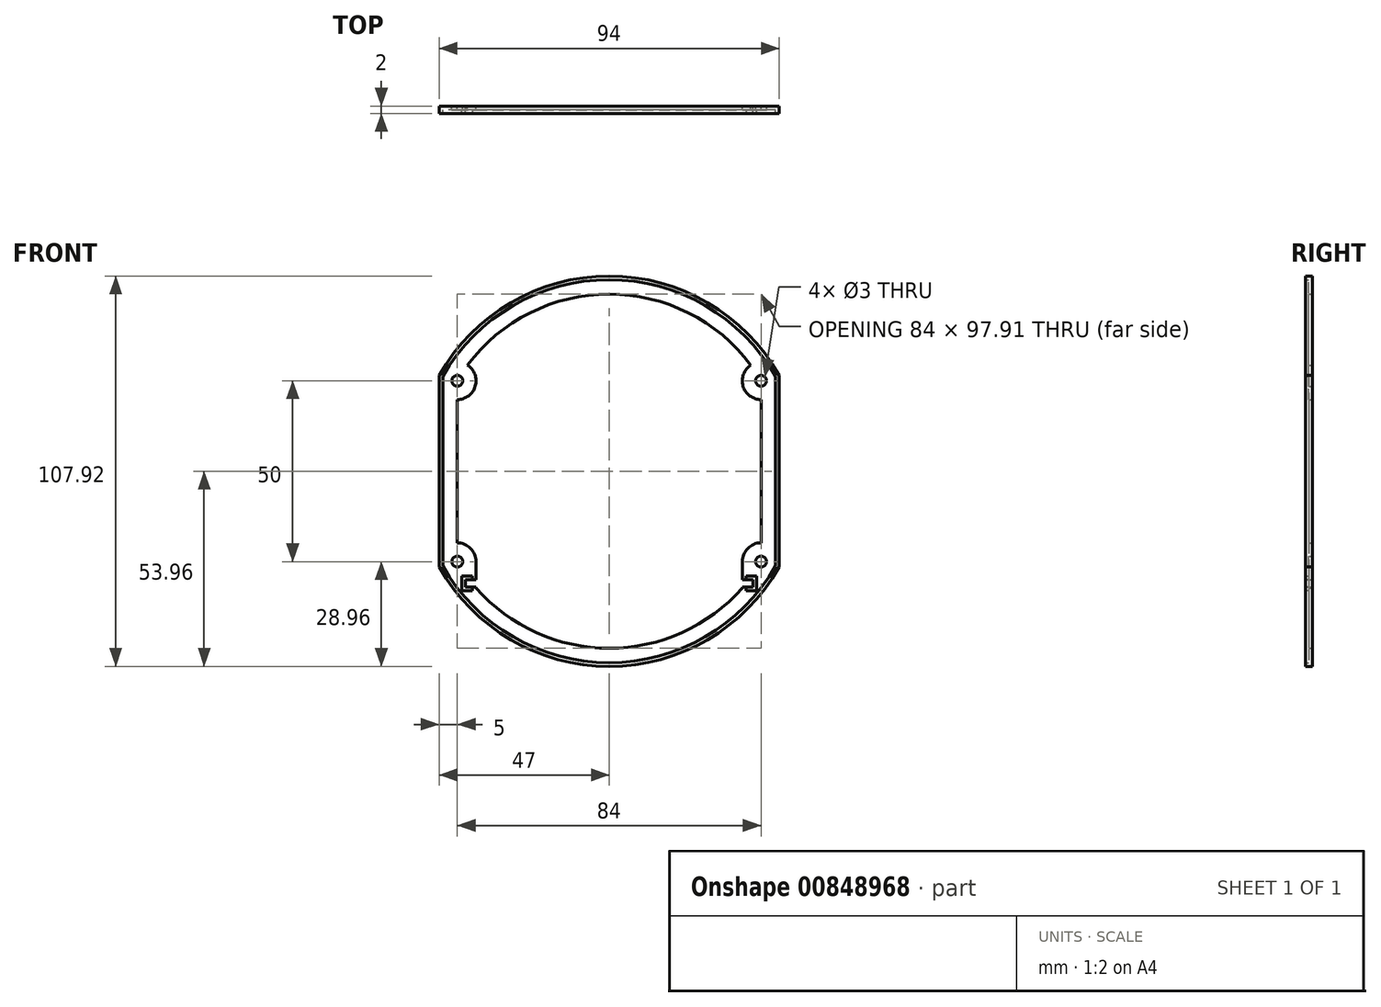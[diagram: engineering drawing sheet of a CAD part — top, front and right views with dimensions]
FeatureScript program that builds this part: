
annotation { "Feature Type Name" : "Feature", "Feature Type Description" : "" }
export const myFeature = defineFeature(function(context is Context, id is Id, definition is map)
    precondition{}
    {
        {
            var Q0;
            Q0=qCreatedBy(makeId("Front.planeOp"),FACE);
            var sketch = newSketch(context, id + "F0", { "sketchPlane" : qUnion([Q0])});
            skPoint(sketch, "E0.middle", {"position": v(0, 0) * mm});
            skCircle(sketch, "E1", {"center": v(-42, 25) * mm, "radius": 1.5 * mm});
            skLineSegment(sketch, "E2.left", {"start": v(-47, 26.5) * mm, "end": v(-47, -26.5) * mm});
            skLineSegment(sketch, "E2.right", {"start": v(47, 26.5) * mm, "end": v(47, -26.5) * mm});
            skArc(sketch, "E3", {"start": v(-39.17, 29.36) * mm, "mid": v(-21.9, 43.78) * mm, "end": v(0, 48.96) * mm});
            skArc(sketch, "E4", {"start": v(-47, 26.5) * mm, "mid": v(-27.22, 46.59) * mm, "end": v(0, 53.96) * mm});
            skArc(sketch, "E5", {"start": v(-39.17, 29.36) * mm, "mid": v(-37.01, 23.53) * mm, "end": v(-42, 19.8) * mm});
            skCircle(sketch, "E6", {"center": v(-42, -25) * mm, "radius": 1.5 * mm});
            skArc(sketch, "E7", {"start": v(-47, -26.5) * mm, "mid": v(-27.22, -46.59) * mm, "end": v(0, -53.96) * mm});
            skLineSegment(sketch, "E8.left", {"start": v(-36.8, -25) * mm, "end": v(-36.8, -30) * mm});
            skLineSegment(sketch, "E9.bottom", {"start": v(-36.8, -30) * mm, "end": v(-39.8, -30) * mm});
            skLineSegment(sketch, "E9.top", {"start": v(-36.8, -32) * mm, "end": v(-39.8, -32) * mm});
            skLineSegment(sketch, "E9.right", {"start": v(-39.8, -30) * mm, "end": v(-39.8, -32) * mm});
            skArc(sketch, "E10", {"start": v(-36.8, -25) * mm, "mid": v(-38.32, -21.32) * mm, "end": v(-42, -19.8) * mm});
            skLineSegment(sketch, "E11", {"start": v(-37.05, -32) * mm, "end": v(-36.8, -32) * mm});
            skLineSegment(sketch, "E12", {"start": v(-36.8, -32.29) * mm, "end": v(-36.8, -32) * mm});
            skArc(sketch, "E13", {"start": v(-36.8, -32.29) * mm, "mid": v(-20.2, -44.6) * mm, "end": v(0, -48.96) * mm});
            skLineSegment(sketch, "E14", {"start": v(-42, 19.8) * mm, "end": v(-42, -19.8) * mm});
            skLineSegment(sketch, "E15", {"start": v(0, 63.92) * mm, "end": v(0, -61.44) * mm, "construction": true});
            skArc(sketch, "E16.MirrorCS", {"start": v(39.17, 29.36) * mm, "mid": v(21.9, 43.78) * mm, "end": v(0, 48.96) * mm});
            skArc(sketch, "E17.MirrorCS", {"start": v(47, 26.5) * mm, "mid": v(27.22, 46.59) * mm, "end": v(0, 53.96) * mm});
            skCircle(sketch, "E18.MirrorC", {"center": v(42, 25) * mm, "radius": 1.5 * mm});
            skArc(sketch, "E19.MirrorCS", {"start": v(39.17, 29.36) * mm, "mid": v(37.01, 23.53) * mm, "end": v(42, 19.8) * mm});
            skArc(sketch, "E20.MirrorCS", {"start": v(36.8, -25) * mm, "mid": v(38.32, -21.32) * mm, "end": v(42, -19.8) * mm});
            skLineSegment(sketch, "E21.MirrorCS", {"start": v(36.8, -25) * mm, "end": v(36.8, -30) * mm});
            skLineSegment(sketch, "E22.MirrorCS", {"start": v(36.8, -30) * mm, "end": v(39.8, -30) * mm});
            skLineSegment(sketch, "E23.MirrorCS", {"start": v(39.8, -30) * mm, "end": v(39.8, -32) * mm});
            skLineSegment(sketch, "E24.MirrorCS", {"start": v(36.8, -32) * mm, "end": v(39.8, -32) * mm});
            skLineSegment(sketch, "E25.MirrorCS", {"start": v(37.05, -32) * mm, "end": v(36.8, -32) * mm});
            skLineSegment(sketch, "E26.MirrorCS", {"start": v(36.8, -32.29) * mm, "end": v(36.8, -32) * mm});
            skLineSegment(sketch, "E27.MirrorCS", {"start": v(42, 19.8) * mm, "end": v(42, -19.8) * mm});
            skArc(sketch, "E28.MirrorCS", {"start": v(36.8, -32.29) * mm, "mid": v(20.2, -44.6) * mm, "end": v(0, -48.96) * mm});
            skArc(sketch, "E29.MirrorCS", {"start": v(47, -26.5) * mm, "mid": v(27.22, -46.59) * mm, "end": v(0, -53.96) * mm});
            skCircle(sketch, "E30.MirrorC", {"center": v(42, -25) * mm, "radius": 1.5 * mm});
            skSolve(sketch);
        }
        {
            var Q0;
            Q0=makeQuery(id+"F0.imprint","IMPRINT",FACE,{"disambiguationData":[TD([[makeQuery(id+"F0.imprint","IMPRINT",EDGE,{"derivedFrom":sQuery(id+"F0.wireOp",EDGE,"E1")}),-1.0]])]});
            extrude(context, id + "F1", {"entities" : qUnion([Q0]), "depth" : 2 * mm, "offsetDistance" : 25 * mm});
        }
        {
            var Q0;
            Q0=makeQuery(id+"F1.opExtrude","CAP_FACE",FACE,{"disambiguationData":[OSD([sQuery(id+"F0.wireOp",EDGE,"E1"),sQuery(id+"F0.wireOp",EDGE,"E2.left"),sQuery(id+"F0.wireOp",EDGE,"E2.right"),sQuery(id+"F0.wireOp",EDGE,"E3"),sQuery(id+"F0.wireOp",EDGE,"E4"),sQuery(id+"F0.wireOp",EDGE,"E5"),sQuery(id+"F0.wireOp",EDGE,"E6"),sQuery(id+"F0.wireOp",EDGE,"E7"),sQuery(id+"F0.wireOp",EDGE,"E8.left"),sQuery(id+"F0.wireOp",EDGE,"E9.bottom"),sQuery(id+"F0.wireOp",EDGE,"E9.top"),sQuery(id+"F0.wireOp",EDGE,"E9.right"),sQuery(id+"F0.wireOp",EDGE,"E10"),sQuery(id+"F0.wireOp",EDGE,"E11"),sQuery(id+"F0.wireOp",EDGE,"E12"),sQuery(id+"F0.wireOp",EDGE,"E13"),sQuery(id+"F0.wireOp",EDGE,"E14"),sQuery(id+"F0.wireOp",EDGE,"E16.MirrorCS"),sQuery(id+"F0.wireOp",EDGE,"E17.MirrorCS"),sQuery(id+"F0.wireOp",EDGE,"E18.MirrorC"),sQuery(id+"F0.wireOp",EDGE,"E19.MirrorCS"),sQuery(id+"F0.wireOp",EDGE,"E20.MirrorCS"),sQuery(id+"F0.wireOp",EDGE,"E21.MirrorCS"),sQuery(id+"F0.wireOp",EDGE,"E22.MirrorCS"),sQuery(id+"F0.wireOp",EDGE,"E23.MirrorCS"),sQuery(id+"F0.wireOp",EDGE,"E24.MirrorCS"),sQuery(id+"F0.wireOp",EDGE,"E25.MirrorCS"),sQuery(id+"F0.wireOp",EDGE,"E26.MirrorCS"),sQuery(id+"F0.wireOp",EDGE,"E27.MirrorCS"),sQuery(id+"F0.wireOp",EDGE,"E28.MirrorCS"),sQuery(id+"F0.wireOp",EDGE,"E29.MirrorCS"),sQuery(id+"F0.wireOp",EDGE,"E30.MirrorC")])],"isStart":false});
            shell(context, id + "F2", {"entities" : qUnion([Q0]), "thickness" : 1 * mm});
        }
        {
            var Q0;
            Q0=makeQuery(id+"F1.opExtrude","CAP_FACE",FACE,{"disambiguationData":[OSD([sQuery(id+"F0.wireOp",EDGE,"E1"),sQuery(id+"F0.wireOp",EDGE,"E2.left"),sQuery(id+"F0.wireOp",EDGE,"E2.right"),sQuery(id+"F0.wireOp",EDGE,"E3"),sQuery(id+"F0.wireOp",EDGE,"E4"),sQuery(id+"F0.wireOp",EDGE,"E5"),sQuery(id+"F0.wireOp",EDGE,"E6"),sQuery(id+"F0.wireOp",EDGE,"E7"),sQuery(id+"F0.wireOp",EDGE,"E8.left"),sQuery(id+"F0.wireOp",EDGE,"E9.bottom"),sQuery(id+"F0.wireOp",EDGE,"E9.top"),sQuery(id+"F0.wireOp",EDGE,"E9.right"),sQuery(id+"F0.wireOp",EDGE,"E10"),sQuery(id+"F0.wireOp",EDGE,"E11"),sQuery(id+"F0.wireOp",EDGE,"E12"),sQuery(id+"F0.wireOp",EDGE,"E13"),sQuery(id+"F0.wireOp",EDGE,"E14"),sQuery(id+"F0.wireOp",EDGE,"E16.MirrorCS"),sQuery(id+"F0.wireOp",EDGE,"E17.MirrorCS"),sQuery(id+"F0.wireOp",EDGE,"E18.MirrorC"),sQuery(id+"F0.wireOp",EDGE,"E19.MirrorCS"),sQuery(id+"F0.wireOp",EDGE,"E20.MirrorCS"),sQuery(id+"F0.wireOp",EDGE,"E21.MirrorCS"),sQuery(id+"F0.wireOp",EDGE,"E22.MirrorCS"),sQuery(id+"F0.wireOp",EDGE,"E23.MirrorCS"),sQuery(id+"F0.wireOp",EDGE,"E24.MirrorCS"),sQuery(id+"F0.wireOp",EDGE,"E25.MirrorCS"),sQuery(id+"F0.wireOp",EDGE,"E26.MirrorCS"),sQuery(id+"F0.wireOp",EDGE,"E27.MirrorCS"),sQuery(id+"F0.wireOp",EDGE,"E28.MirrorCS"),sQuery(id+"F0.wireOp",EDGE,"E29.MirrorCS"),sQuery(id+"F0.wireOp",EDGE,"E30.MirrorC")])],"isStart":false});
            var sketch = newSketch(context, id + "F3", { "sketchPlane" : qUnion([Q0])});
            skLineSegment(sketch, "E31.bottom", {"start": v(-40.8, -29) * mm, "end": v(-37.8, -29) * mm});
            skLineSegment(sketch, "E31.top", {"start": v(-40.8, -33) * mm, "end": v(-37.8, -33) * mm});
            skLineSegment(sketch, "E31.left", {"start": v(-40.8, -29) * mm, "end": v(-40.8, -33) * mm});
            skLineSegment(sketch, "E31.right", {"start": v(-37.8, -29) * mm, "end": v(-37.8, -33) * mm});
            skLineSegment(sketch, "E32.bottom", {"start": v(40.8, -29) * mm, "end": v(37.8, -29) * mm});
            skLineSegment(sketch, "E32.top", {"start": v(40.8, -33) * mm, "end": v(37.8, -33) * mm});
            skLineSegment(sketch, "E32.left", {"start": v(40.8, -29) * mm, "end": v(40.8, -33) * mm});
            skLineSegment(sketch, "E32.right", {"start": v(37.8, -29) * mm, "end": v(37.8, -33) * mm});
            skSolve(sketch);
        }
        {
            var Q0;
            {var subQ0=sQuery(id+"F0.wireOp",EDGE,"E30.MirrorC");var subQ1=sQuery(id+"F0.wireOp",EDGE,"E29.MirrorCS");var subQ2=sQuery(id+"F0.wireOp",EDGE,"E28.MirrorCS");var subQ3=sQuery(id+"F0.wireOp",EDGE,"E27.MirrorCS");var subQ4=sQuery(id+"F0.wireOp",EDGE,"E26.MirrorCS");var subQ5=sQuery(id+"F0.wireOp",EDGE,"E25.MirrorCS");var subQ6=sQuery(id+"F0.wireOp",EDGE,"E24.MirrorCS");var subQ7=sQuery(id+"F0.wireOp",EDGE,"E23.MirrorCS");var subQ8=sQuery(id+"F0.wireOp",EDGE,"E22.MirrorCS");var subQ9=sQuery(id+"F0.wireOp",EDGE,"E21.MirrorCS");var subQ10=sQuery(id+"F0.wireOp",EDGE,"E20.MirrorCS");var subQ11=sQuery(id+"F0.wireOp",EDGE,"E19.MirrorCS");var subQ12=sQuery(id+"F0.wireOp",EDGE,"E18.MirrorC");var subQ13=sQuery(id+"F0.wireOp",EDGE,"E17.MirrorCS");var subQ14=sQuery(id+"F0.wireOp",EDGE,"E16.MirrorCS");var subQ15=sQuery(id+"F0.wireOp",EDGE,"E14");var subQ16=sQuery(id+"F0.wireOp",EDGE,"E13");var subQ17=sQuery(id+"F0.wireOp",EDGE,"E12");var subQ18=sQuery(id+"F0.wireOp",EDGE,"E11");var subQ19=sQuery(id+"F0.wireOp",EDGE,"E10");var subQ20=sQuery(id+"F0.wireOp",EDGE,"E9.right");var subQ21=sQuery(id+"F0.wireOp",EDGE,"E9.top");var subQ22=sQuery(id+"F0.wireOp",EDGE,"E9.bottom");var subQ23=sQuery(id+"F0.wireOp",EDGE,"E8.left");var subQ24=sQuery(id+"F0.wireOp",EDGE,"E7");var subQ25=sQuery(id+"F0.wireOp",EDGE,"E6");var subQ26=sQuery(id+"F0.wireOp",EDGE,"E5");var subQ27=sQuery(id+"F0.wireOp",EDGE,"E4");var subQ28=sQuery(id+"F0.wireOp",EDGE,"E3");var subQ29=sQuery(id+"F0.wireOp",EDGE,"E2.right");var subQ30=sQuery(id+"F0.wireOp",EDGE,"E2.left");var subQ31=sQuery(id+"F0.wireOp",EDGE,"E1");Q0=makeQuery(id+"F2.opShell","OFFSET_FACE",FACE,{"disambiguationData":[OSD([subQ31,subQ30,subQ29,subQ28,subQ27,subQ26,subQ25,subQ24,subQ23,subQ22,subQ21,subQ20,subQ19,subQ18,subQ17,subQ16,subQ15,subQ14,subQ13,subQ12,subQ11,subQ10,subQ9,subQ8,subQ7,subQ6,subQ5,subQ4,subQ3,subQ2,subQ1,subQ0]),TDD([makeQuery(id+"F1.opExtrude","CAP_FACE",FACE,{"disambiguationData":[OSD([subQ31,subQ30,subQ29,subQ28,subQ27,subQ26,subQ25,subQ24,subQ23,subQ22,subQ21,subQ20,subQ19,subQ18,subQ17,subQ16,subQ15,subQ14,subQ13,subQ12,subQ11,subQ10,subQ9,subQ8,subQ7,subQ6,subQ5,subQ4,subQ3,subQ2,subQ1,subQ0])],"isStart":false})]),OD(0.0)]});}
            var Q1;
            {var subQ0=sQuery(id+"F0.wireOp",EDGE,"E30.MirrorC");var subQ1=sQuery(id+"F0.wireOp",EDGE,"E29.MirrorCS");var subQ2=sQuery(id+"F0.wireOp",EDGE,"E28.MirrorCS");var subQ3=sQuery(id+"F0.wireOp",EDGE,"E27.MirrorCS");var subQ4=sQuery(id+"F0.wireOp",EDGE,"E26.MirrorCS");var subQ5=sQuery(id+"F0.wireOp",EDGE,"E25.MirrorCS");var subQ6=sQuery(id+"F0.wireOp",EDGE,"E24.MirrorCS");var subQ7=sQuery(id+"F0.wireOp",EDGE,"E23.MirrorCS");var subQ8=sQuery(id+"F0.wireOp",EDGE,"E22.MirrorCS");var subQ9=sQuery(id+"F0.wireOp",EDGE,"E21.MirrorCS");var subQ10=sQuery(id+"F0.wireOp",EDGE,"E20.MirrorCS");var subQ11=sQuery(id+"F0.wireOp",EDGE,"E19.MirrorCS");var subQ12=sQuery(id+"F0.wireOp",EDGE,"E18.MirrorC");var subQ13=sQuery(id+"F0.wireOp",EDGE,"E17.MirrorCS");var subQ14=sQuery(id+"F0.wireOp",EDGE,"E16.MirrorCS");var subQ15=sQuery(id+"F0.wireOp",EDGE,"E14");var subQ16=sQuery(id+"F0.wireOp",EDGE,"E13");var subQ17=sQuery(id+"F0.wireOp",EDGE,"E12");var subQ18=sQuery(id+"F0.wireOp",EDGE,"E11");var subQ19=sQuery(id+"F0.wireOp",EDGE,"E10");var subQ20=sQuery(id+"F0.wireOp",EDGE,"E9.right");var subQ21=sQuery(id+"F0.wireOp",EDGE,"E9.top");var subQ22=sQuery(id+"F0.wireOp",EDGE,"E9.bottom");var subQ23=sQuery(id+"F0.wireOp",EDGE,"E8.left");var subQ24=sQuery(id+"F0.wireOp",EDGE,"E7");var subQ25=sQuery(id+"F0.wireOp",EDGE,"E6");var subQ26=sQuery(id+"F0.wireOp",EDGE,"E5");var subQ27=sQuery(id+"F0.wireOp",EDGE,"E4");var subQ28=sQuery(id+"F0.wireOp",EDGE,"E3");var subQ29=sQuery(id+"F0.wireOp",EDGE,"E2.right");var subQ30=sQuery(id+"F0.wireOp",EDGE,"E2.left");var subQ31=sQuery(id+"F0.wireOp",EDGE,"E1");Q1=makeQuery(id+"F2.opShell","OFFSET_FACE",FACE,{"disambiguationData":[OSD([subQ31,subQ30,subQ29,subQ28,subQ27,subQ26,subQ25,subQ24,subQ23,subQ22,subQ21,subQ20,subQ19,subQ18,subQ17,subQ16,subQ15,subQ14,subQ13,subQ12,subQ11,subQ10,subQ9,subQ8,subQ7,subQ6,subQ5,subQ4,subQ3,subQ2,subQ1,subQ0]),TDD([makeQuery(id+"F1.opExtrude","CAP_FACE",FACE,{"disambiguationData":[OSD([subQ31,subQ30,subQ29,subQ28,subQ27,subQ26,subQ25,subQ24,subQ23,subQ22,subQ21,subQ20,subQ19,subQ18,subQ17,subQ16,subQ15,subQ14,subQ13,subQ12,subQ11,subQ10,subQ9,subQ8,subQ7,subQ6,subQ5,subQ4,subQ3,subQ2,subQ1,subQ0])],"isStart":false})]),OD(3.0)]});}
            var Q2;
            {var subQ0=sQuery(id+"F0.wireOp",EDGE,"E30.MirrorC");var subQ1=sQuery(id+"F0.wireOp",EDGE,"E29.MirrorCS");var subQ2=sQuery(id+"F0.wireOp",EDGE,"E28.MirrorCS");var subQ3=sQuery(id+"F0.wireOp",EDGE,"E27.MirrorCS");var subQ4=sQuery(id+"F0.wireOp",EDGE,"E26.MirrorCS");var subQ5=sQuery(id+"F0.wireOp",EDGE,"E25.MirrorCS");var subQ6=sQuery(id+"F0.wireOp",EDGE,"E24.MirrorCS");var subQ7=sQuery(id+"F0.wireOp",EDGE,"E23.MirrorCS");var subQ8=sQuery(id+"F0.wireOp",EDGE,"E22.MirrorCS");var subQ9=sQuery(id+"F0.wireOp",EDGE,"E21.MirrorCS");var subQ10=sQuery(id+"F0.wireOp",EDGE,"E20.MirrorCS");var subQ11=sQuery(id+"F0.wireOp",EDGE,"E19.MirrorCS");var subQ12=sQuery(id+"F0.wireOp",EDGE,"E18.MirrorC");var subQ13=sQuery(id+"F0.wireOp",EDGE,"E17.MirrorCS");var subQ14=sQuery(id+"F0.wireOp",EDGE,"E16.MirrorCS");var subQ15=sQuery(id+"F0.wireOp",EDGE,"E14");var subQ16=sQuery(id+"F0.wireOp",EDGE,"E13");var subQ17=sQuery(id+"F0.wireOp",EDGE,"E12");var subQ18=sQuery(id+"F0.wireOp",EDGE,"E11");var subQ19=sQuery(id+"F0.wireOp",EDGE,"E10");var subQ20=sQuery(id+"F0.wireOp",EDGE,"E9.right");var subQ21=sQuery(id+"F0.wireOp",EDGE,"E9.top");var subQ22=sQuery(id+"F0.wireOp",EDGE,"E9.bottom");var subQ23=sQuery(id+"F0.wireOp",EDGE,"E8.left");var subQ24=sQuery(id+"F0.wireOp",EDGE,"E7");var subQ25=sQuery(id+"F0.wireOp",EDGE,"E6");var subQ26=sQuery(id+"F0.wireOp",EDGE,"E5");var subQ27=sQuery(id+"F0.wireOp",EDGE,"E4");var subQ28=sQuery(id+"F0.wireOp",EDGE,"E3");var subQ29=sQuery(id+"F0.wireOp",EDGE,"E2.right");var subQ30=sQuery(id+"F0.wireOp",EDGE,"E2.left");var subQ31=sQuery(id+"F0.wireOp",EDGE,"E1");Q2=makeQuery(id+"F2.opShell","OFFSET_FACE",FACE,{"disambiguationData":[OSD([subQ31,subQ30,subQ29,subQ28,subQ27,subQ26,subQ25,subQ24,subQ23,subQ22,subQ21,subQ20,subQ19,subQ18,subQ17,subQ16,subQ15,subQ14,subQ13,subQ12,subQ11,subQ10,subQ9,subQ8,subQ7,subQ6,subQ5,subQ4,subQ3,subQ2,subQ1,subQ0]),TDD([makeQuery(id+"F1.opExtrude","CAP_FACE",FACE,{"disambiguationData":[OSD([subQ31,subQ30,subQ29,subQ28,subQ27,subQ26,subQ25,subQ24,subQ23,subQ22,subQ21,subQ20,subQ19,subQ18,subQ17,subQ16,subQ15,subQ14,subQ13,subQ12,subQ11,subQ10,subQ9,subQ8,subQ7,subQ6,subQ5,subQ4,subQ3,subQ2,subQ1,subQ0])],"isStart":false})]),OD(4.0)]});}
            var Q3;
            {var subQ0=sQuery(id+"F0.wireOp",EDGE,"E30.MirrorC");var subQ1=sQuery(id+"F0.wireOp",EDGE,"E29.MirrorCS");var subQ2=sQuery(id+"F0.wireOp",EDGE,"E28.MirrorCS");var subQ3=sQuery(id+"F0.wireOp",EDGE,"E27.MirrorCS");var subQ4=sQuery(id+"F0.wireOp",EDGE,"E26.MirrorCS");var subQ5=sQuery(id+"F0.wireOp",EDGE,"E25.MirrorCS");var subQ6=sQuery(id+"F0.wireOp",EDGE,"E24.MirrorCS");var subQ7=sQuery(id+"F0.wireOp",EDGE,"E23.MirrorCS");var subQ8=sQuery(id+"F0.wireOp",EDGE,"E22.MirrorCS");var subQ9=sQuery(id+"F0.wireOp",EDGE,"E21.MirrorCS");var subQ10=sQuery(id+"F0.wireOp",EDGE,"E20.MirrorCS");var subQ11=sQuery(id+"F0.wireOp",EDGE,"E19.MirrorCS");var subQ12=sQuery(id+"F0.wireOp",EDGE,"E18.MirrorC");var subQ13=sQuery(id+"F0.wireOp",EDGE,"E17.MirrorCS");var subQ14=sQuery(id+"F0.wireOp",EDGE,"E16.MirrorCS");var subQ15=sQuery(id+"F0.wireOp",EDGE,"E14");var subQ16=sQuery(id+"F0.wireOp",EDGE,"E13");var subQ17=sQuery(id+"F0.wireOp",EDGE,"E12");var subQ18=sQuery(id+"F0.wireOp",EDGE,"E11");var subQ19=sQuery(id+"F0.wireOp",EDGE,"E10");var subQ20=sQuery(id+"F0.wireOp",EDGE,"E9.right");var subQ21=sQuery(id+"F0.wireOp",EDGE,"E9.top");var subQ22=sQuery(id+"F0.wireOp",EDGE,"E9.bottom");var subQ23=sQuery(id+"F0.wireOp",EDGE,"E8.left");var subQ24=sQuery(id+"F0.wireOp",EDGE,"E7");var subQ25=sQuery(id+"F0.wireOp",EDGE,"E6");var subQ26=sQuery(id+"F0.wireOp",EDGE,"E5");var subQ27=sQuery(id+"F0.wireOp",EDGE,"E4");var subQ28=sQuery(id+"F0.wireOp",EDGE,"E3");var subQ29=sQuery(id+"F0.wireOp",EDGE,"E2.right");var subQ30=sQuery(id+"F0.wireOp",EDGE,"E2.left");var subQ31=sQuery(id+"F0.wireOp",EDGE,"E1");Q3=makeQuery(id+"F2.opShell","OFFSET_FACE",FACE,{"disambiguationData":[OSD([subQ31,subQ30,subQ29,subQ28,subQ27,subQ26,subQ25,subQ24,subQ23,subQ22,subQ21,subQ20,subQ19,subQ18,subQ17,subQ16,subQ15,subQ14,subQ13,subQ12,subQ11,subQ10,subQ9,subQ8,subQ7,subQ6,subQ5,subQ4,subQ3,subQ2,subQ1,subQ0]),TDD([makeQuery(id+"F1.opExtrude","CAP_FACE",FACE,{"disambiguationData":[OSD([subQ31,subQ30,subQ29,subQ28,subQ27,subQ26,subQ25,subQ24,subQ23,subQ22,subQ21,subQ20,subQ19,subQ18,subQ17,subQ16,subQ15,subQ14,subQ13,subQ12,subQ11,subQ10,subQ9,subQ8,subQ7,subQ6,subQ5,subQ4,subQ3,subQ2,subQ1,subQ0])],"isStart":false})]),OD(2.0)]});}
            var Q4;
            {var subQ1=sQuery(id+"F3.wireOp",EDGE,"E31.bottom");Q4=makeQuery(id+"F3.imprint","IMPRINT",FACE,{"disambiguationData":[TD([[makeQuery(id+"F3.imprint","IMPRINT",EDGE,{"derivedFrom":subQ1}),1.0]])]});}
            var Q5;
            {var subQ1=sQuery(id+"F3.wireOp",EDGE,"E32.bottom");Q5=makeQuery(id+"F3.imprint","IMPRINT",FACE,{"disambiguationData":[TD([[makeQuery(id+"F3.imprint","IMPRINT",EDGE,{"derivedFrom":subQ1}),-1.0]])]});}
            extrude(context, id + "F4", {"entities" : qUnion([Q0, Q1, Q2, Q3, Q4, Q5]), "operationType" : NewBodyOperationType.REMOVE, "oppositeDirection" : true, "depth" : 1 * mm, "offsetDistance" : 25 * mm});
        }
    });
